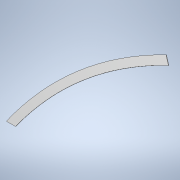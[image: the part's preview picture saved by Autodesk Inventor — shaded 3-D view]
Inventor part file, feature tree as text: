
AUTODESK INVENTOR PART (.ipt)
format: ipt  version: 2021 (Build 250183000, 183)  size: 113,664 bytes
history: native  units: in
note: dims shown in document units (in); Inventor stores cm internally (conversion verified against a paired STEP export)
features: sketch x2, sweep x1
ambient origin geometry x8: Origin, YZ Plane, XZ Plane, XY Plane, X Axis, Y Axis, Z Axis, Center Point
bodies: Solid1 (feature_tree)
feature tree (3):
  sweep  "Sweep1"
  sketch  "Sketch1"  dims[d0=2.0in d1=0.1in d4=0.0in d5=0.0in]
  sketch  "3D Sketch1"
